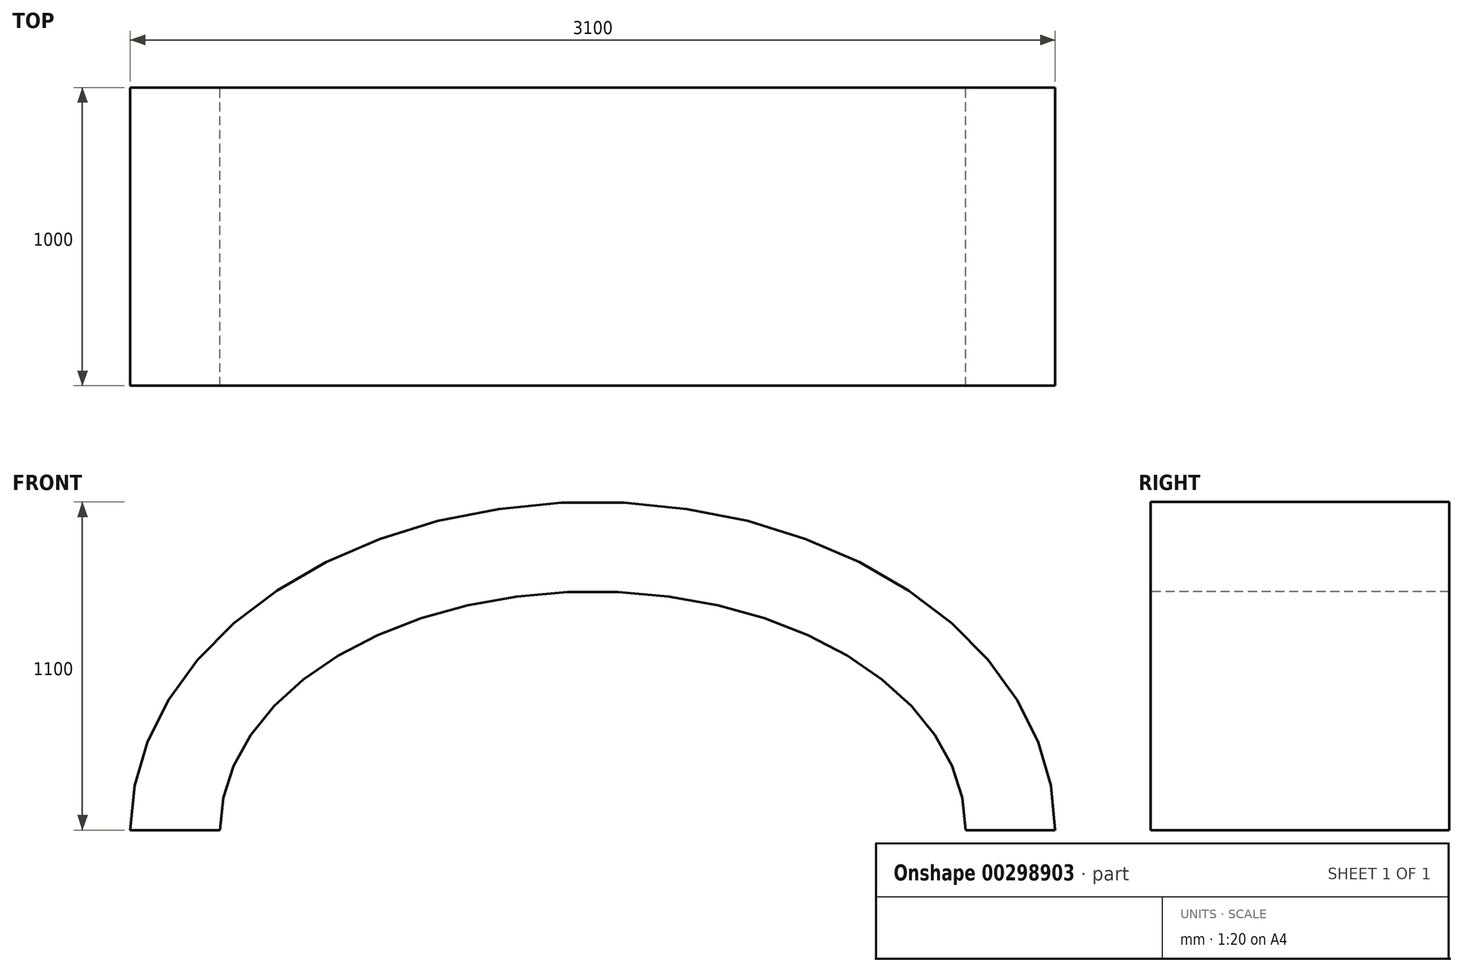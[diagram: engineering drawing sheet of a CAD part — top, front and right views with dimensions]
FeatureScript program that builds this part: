
annotation { "Feature Type Name" : "Feature", "Feature Type Description" : "" }
export const myFeature = defineFeature(function(context is Context, id is Id, definition is map)
    precondition{}
    {
        {
            var Q0;
            Q0=qCreatedBy(makeId("Front.planeOp"),FACE);
            var sketch = newSketch(context, id + "F0", { "sketchPlane" : qUnion([Q0])});
            skLineSegment(sketch, "E0.bottom", {"start": v(0, 0) * mm, "end": v(2500, 0) * mm});
            skLineSegment(sketch, "E0.top", {"start": v(0, -1500) * mm, "end": v(2500, -1500) * mm});
            skLineSegment(sketch, "E0.left", {"start": v(0, 0) * mm, "end": v(0, -1500) * mm});
            skLineSegment(sketch, "E0.right", {"start": v(2500, 0) * mm, "end": v(2500, -1500) * mm});
            skLineSegment(sketch, "E1", {"start": v(1250, 0) * mm, "end": v(1250, 800) * mm, "construction": true});
            skEllipticalArc(sketch, "E2", {});
            skLineSegment(sketch, "E3", {"start": v(1250, 800) * mm, "end": v(1250, 1100) * mm, "construction": true});
            skLineSegment(sketch, "E4", {"start": v(2500, 0) * mm, "end": v(2800, 0) * mm});
            skLineSegment(sketch, "E5", {"start": v(0, 0) * mm, "end": v(-300, 0) * mm});
            skEllipticalArc(sketch, "E6.trimOffspring", {});
            const initialGuessF0  = {"E2": [1.25, 0, -1, 0, 1.25, 0.8, 3.141592653589793, 0], "E6.trimOffspring": [1.25, 0, 1, 0, 1.55, 1.1, 0, 3.141592653589793]};
            skSetInitialGuess(sketch, initialGuessF0);
            skSolve(sketch);
        }
        {
            var Q0;
            Q0=makeQuery(id+"F0.imprint","IMPRINT",FACE,{"disambiguationData":[TD([[makeQuery(id+"F0.imprint","IMPRINT",EDGE,{"derivedFrom":sQuery(id+"F0.wireOp",EDGE,"E2")}),-1.0]])]});
            extrude(context, id + "F1", {"entities" : qUnion([Q0]), "depth" : 1000 * mm});
        }
    });
